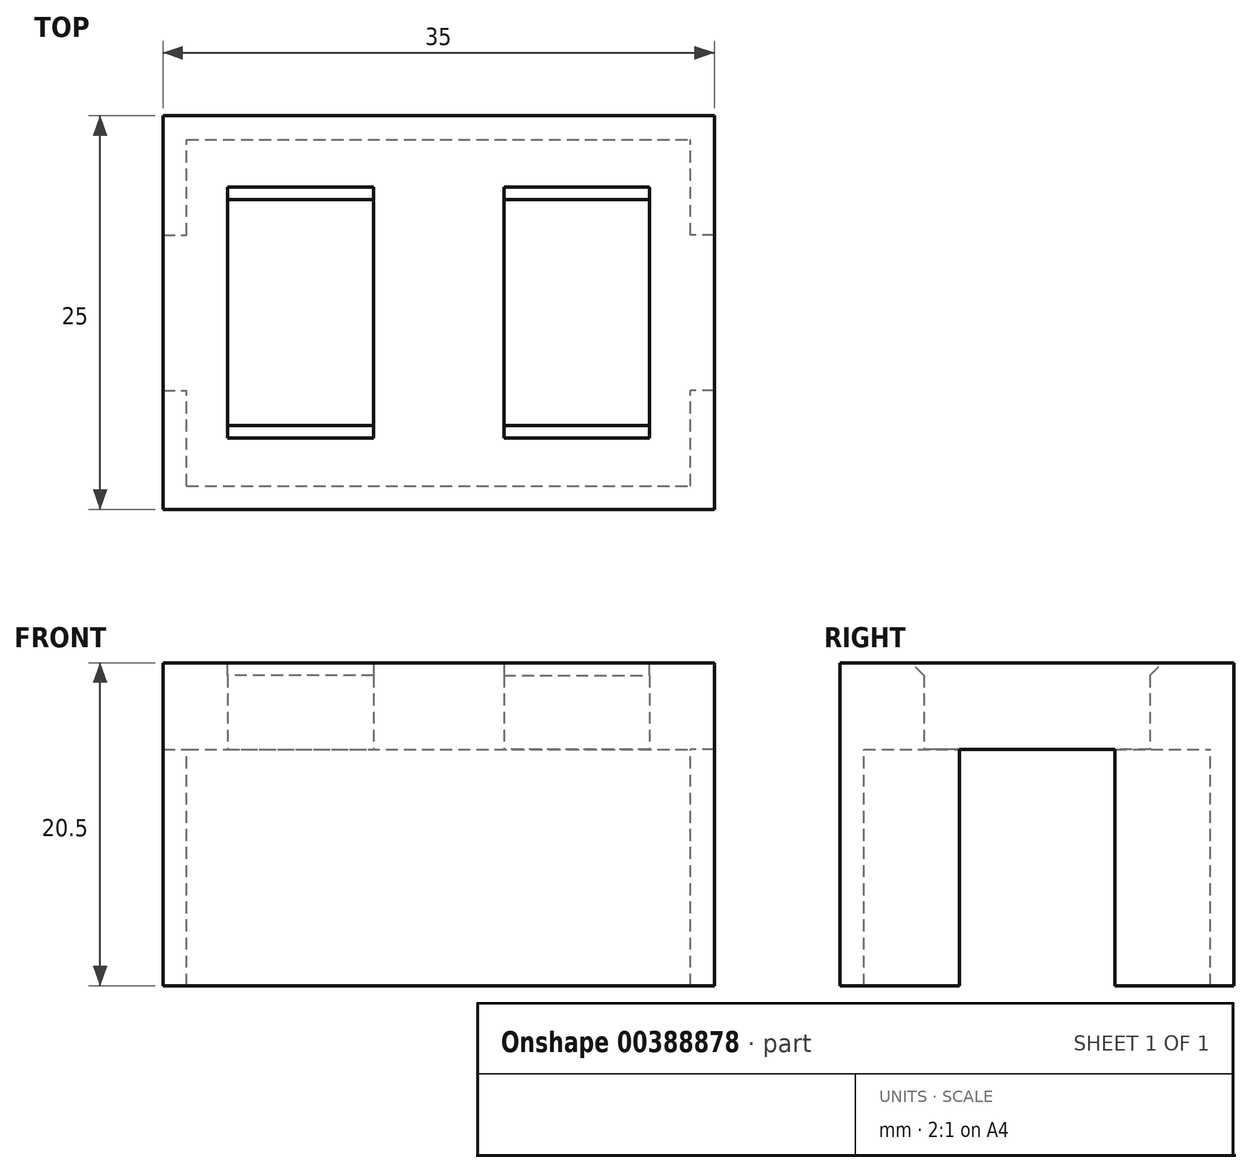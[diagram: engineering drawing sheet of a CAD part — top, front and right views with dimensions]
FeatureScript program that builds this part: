
annotation { "Feature Type Name" : "Feature", "Feature Type Description" : "" }
export const myFeature = defineFeature(function(context is Context, id is Id, definition is map)
    precondition{}
    {
        {
            var Q0;
            Q0=qCreatedBy(makeId("Top.planeOp"),FACE);
            var sketch = newSketch(context, id + "F0", { "sketchPlane" : qUnion([Q0])});
            skLineSegment(sketch, "E0.bottom", {"start": v(0, 0) * mm, "end": v(35, 0) * mm});
            skLineSegment(sketch, "E0.top", {"start": v(0, 25) * mm, "end": v(35, 25) * mm});
            skLineSegment(sketch, "E0.left", {"start": v(0, 0) * mm, "end": v(0, 25) * mm});
            skLineSegment(sketch, "E0.right", {"start": v(35, 0) * mm, "end": v(35, 25) * mm});
            skLineSegment(sketch, "E1", {"start": v(17.5, 25) * mm, "end": v(17.5, 0) * mm, "construction": true});
            skLineSegment(sketch, "E2.bottom", {"start": v(4.1, 19.68) * mm, "end": v(13.36, 19.68) * mm});
            skLineSegment(sketch, "E2.top", {"start": v(4.1, 5.33) * mm, "end": v(13.36, 5.33) * mm});
            skLineSegment(sketch, "E2.left", {"start": v(4.1, 19.68) * mm, "end": v(4.1, 5.33) * mm});
            skLineSegment(sketch, "E2.right", {"start": v(13.36, 19.68) * mm, "end": v(13.36, 5.33) * mm});
            skLineSegment(sketch, "E3", {"start": v(8.73, 25) * mm, "end": v(8.73, 19.68) * mm, "construction": true});
            skPoint(sketch, "E3.startSnap0", {"position": v(8.73, 19.68) * mm});
            skLineSegment(sketch, "E4", {"start": v(8.73, 19.68) * mm, "end": v(8.73, 5.33) * mm, "construction": true});
            skLineSegment(sketch, "E5", {"start": v(8.73, 5.33) * mm, "end": v(8.73, 0) * mm, "construction": true});
            skLineSegment(sketch, "E6.MirrorCS", {"start": v(26.27, 25) * mm, "end": v(26.27, 19.68) * mm, "construction": true});
            skPoint(sketch, "E7.MirrorP", {"position": v(26.27, 19.68) * mm});
            skLineSegment(sketch, "E8.MirrorCS", {"start": v(26.27, 5.33) * mm, "end": v(26.27, 0) * mm, "construction": true});
            skLineSegment(sketch, "E9.MirrorCS", {"start": v(26.27, 19.68) * mm, "end": v(26.27, 5.33) * mm, "construction": true});
            skLineSegment(sketch, "E10.MirrorCS", {"start": v(21.64, 19.68) * mm, "end": v(21.64, 5.33) * mm});
            skLineSegment(sketch, "E11.MirrorCS", {"start": v(30.9, 19.68) * mm, "end": v(30.9, 5.33) * mm});
            skLineSegment(sketch, "E12.MirrorCS", {"start": v(30.9, 5.33) * mm, "end": v(21.64, 5.33) * mm});
            skLineSegment(sketch, "E13.MirrorCS", {"start": v(30.9, 19.68) * mm, "end": v(21.64, 19.68) * mm});
            skSolve(sketch);
        }
        {
            var Q0;
            Q0 = qSketchRegion(id + "F0", true);
            extrude(context, id + "F1", {"entities" : qUnion([Q0]), "depth" : 5.5 * mm});
        }
        {
            var Q0;
            Q0=makeQuery(id+"F1.opExtrude","CAP_FACE",FACE,{"disambiguationData":[OSD([sQuery(id+"F0.wireOp",EDGE,"E0.bottom"),sQuery(id+"F0.wireOp",EDGE,"E0.top"),sQuery(id+"F0.wireOp",EDGE,"E0.left"),sQuery(id+"F0.wireOp",EDGE,"E0.right"),sQuery(id+"F0.wireOp",EDGE,"E2.bottom"),sQuery(id+"F0.wireOp",EDGE,"E2.top"),sQuery(id+"F0.wireOp",EDGE,"E2.left"),sQuery(id+"F0.wireOp",EDGE,"E2.right"),sQuery(id+"F0.wireOp",EDGE,"E10.MirrorCS"),sQuery(id+"F0.wireOp",EDGE,"E11.MirrorCS"),sQuery(id+"F0.wireOp",EDGE,"E12.MirrorCS"),sQuery(id+"F0.wireOp",EDGE,"E13.MirrorCS")])],"isStart":true});
            var sketch = newSketch(context, id + "F2", { "sketchPlane" : qUnion([Q0])});
            skLineSegment(sketch, "E14.0", {"start": v(0, 0) * mm, "end": v(0, -25) * mm});
            skLineSegment(sketch, "E15.0", {"start": v(0, 0) * mm, "end": v(35, 0) * mm});
            skLineSegment(sketch, "E16.0", {"start": v(35, 0) * mm, "end": v(35, -25) * mm});
            skLineSegment(sketch, "E17.0", {"start": v(0, -25) * mm, "end": v(35, -25) * mm});
            skLineSegment(sketch, "E18.0", {"start": v(1.5, -1.5) * mm, "end": v(33.5, -1.5) * mm});
            skLineSegment(sketch, "E18.1", {"start": v(1.5, -1.5) * mm, "end": v(1.5, -23.5) * mm});
            skLineSegment(sketch, "E18.2", {"start": v(1.5, -23.5) * mm, "end": v(33.5, -23.5) * mm});
            skLineSegment(sketch, "E18.3", {"start": v(33.5, -1.5) * mm, "end": v(33.5, -23.5) * mm});
            skLineSegment(sketch, "E19", {"start": v(0, -12.5) * mm, "end": v(35, -12.5) * mm, "construction": true});
            skLineSegment(sketch, "E20", {"start": v(0, -7.56) * mm, "end": v(1.5, -7.56) * mm});
            skLineSegment(sketch, "E21.MirrorCS", {"start": v(0, -17.44) * mm, "end": v(1.5, -17.44) * mm});
            skLineSegment(sketch, "E22", {"start": v(17.5, -1.5) * mm, "end": v(17.5, -23.5) * mm, "construction": true});
            skLineSegment(sketch, "E23.MirrorCS", {"start": v(35, -7.56) * mm, "end": v(33.5, -7.56) * mm});
            skLineSegment(sketch, "E24.MirrorCS", {"start": v(35, -17.44) * mm, "end": v(33.5, -17.44) * mm});
            skSolve(sketch);
        }
        {
            var Q0;
            {var subQ1=sQuery(id+"F2.wireOp",EDGE,"E15.0");Q0=makeQuery(id+"F2.imprint","IMPRINT",FACE,{"disambiguationData":[TD([[makeQuery(id+"F2.imprint","IMPRINT",EDGE,{"derivedFrom":subQ1}),-1.0]])]});}
            var Q1;
            {var subQ3=sQuery(id+"F2.wireOp",EDGE,"E17.0");Q1=makeQuery(id+"F2.imprint","IMPRINT",FACE,{"disambiguationData":[TD([[makeQuery(id+"F2.imprint","IMPRINT",EDGE,{"derivedFrom":subQ3}),1.0]])]});}
            extrude(context, id + "F3", {"entities" : qUnion([Q0, Q1]), "operationType" : NewBodyOperationType.ADD, "depth" : 15 * mm});
        }
        {
            var Q0;
            Q0=makeQuery(id+"F1.opExtrude","CAP_EDGE",EDGE,{"disambiguationData":[OSD([sQuery(id+"F0.wireOp",EDGE,"E2.bottom")])],"isStart":false});
            var Q1;
            Q1=makeQuery(id+"F1.opExtrude","CAP_EDGE",EDGE,{"disambiguationData":[OSD([sQuery(id+"F0.wireOp",EDGE,"E2.top")])],"isStart":false});
            var Q2;
            Q2=makeQuery(id+"F1.opExtrude","CAP_EDGE",EDGE,{"disambiguationData":[OSD([sQuery(id+"F0.wireOp",EDGE,"E13.MirrorCS")])],"isStart":false});
            var Q3;
            Q3=makeQuery(id+"F1.opExtrude","CAP_EDGE",EDGE,{"disambiguationData":[OSD([sQuery(id+"F0.wireOp",EDGE,"E12.MirrorCS")])],"isStart":false});
            chamfer(context, id + "F4", {"entities" : qUnion([Q0, Q1, Q2, Q3]), "width" : .8 * mm, "tangentPropagation" : true});
        }
    });
